# Revit family: Legrand XL³-S 630 16 Modules to the row
name_source: partatom
category: Equipement électrique
units: mm (PartAtom-declared; Revit-internal decimal feet)

## family parameters
Basée sur le plan de construction = Non
Configuration du panneau = Deux colonnes, circuits au sein
Cote de connecteur circulaire = Utiliser le diamètre
Couper avec des vides une fois chargée = Non
Numéro OmniClass = 23.80.30.11.17
Partagée = Non
Point de calcul de pièce = Non
Titre OmniClass = Distribution Boards and Control Panels
Toujours verticalement = Oui
Type d'élément = Tableau de raccordement

## types (11) — shared parameters
ETIM Class 6.0 = EC000261
Fabricant = Legrand
General Conditions of Use = https://export.legrand.com
IK = 08
IP = 40
Image du type = XL3S_630_16M_337581_p_230129.jpg
Material = Steel
RAL = 9003
URL = www.legrand.fr
depth = 249 mm  [stored 0.816929 ft]
depth installation zone = 703 mm  [stored 2.30643 ft]
distance before installation zone = 454 mm  [stored 1.4895 ft]
distance side installation zone = 249 mm  [stored 0.816929 ft]
door = Oui
finish kit = Non
finish kit 337960_337972 = Non
finish kit 337961_337972 = Non
finish kit 337962_337972 = Non
finish kit 337963_337972 = Non
finish kit 337964_337972 = Non
finish kit 337965_337972 = Non
finish kit 337966_337972 = Non
finish kit 337967_337972 = Non
finish kit 337968_337972 = Non
finish kit 337969_337972 = Non
finish kit 337970_337972 = Non
height Base = 100 mm  [stored 0.328084 ft]
left side panel = Oui
plinth = Oui
right side panel = Oui
width = 454 mm  [stored 1.4895 ft]
width installation zone = 952 mm  [stored 3.12336 ft]
zero-valued in all types: Elévation par défaut

## per-type parameters (varying)
- Distribution envelope - XL³ S 630 Métal - height 750 - 16 modules: Description=337521  Distribution envelope - XL³ S 630 Métal - height 750 - 16 modules; door 337641=Oui; door 337651=Non; door 337661=Non; door 337671=Non; door 337681=Non; door 337691=Non; door 337701=Non; door 337711=Non; door 337721=Non; door 337731=Non; door 337741=Non; envelope 337521=Oui; envelope 337531=Non; envelope 337541=Non; envelope 337551=Non; envelope 337561=Non; envelope 337571=Non; envelope 337581=Non; envelope 337591=Non; envelope 337601=Non; envelope 337611=Non; envelope 337621=Non; height=924 mm  [stored 3.0315 ft]; left side panel  337872=Non; left side panel 337862=Oui; left side panel 337863=Non; left side panel 337864=Non; left side panel 337865=Non; left side panel 337866=Non; left side panel 337867=Non; left side panel 337868=Non; left side panel 337869=Non; left side panel 337870=Non; left side panel 337871=Non; right side panel 337862=Oui; right side panel 337863=Non; right side panel 337864=Non; right side panel 337865=Non; right side panel 337866=Non; right side panel 337867=Non; right side panel 337868=Non; right side panel 337869=Non; right side panel 337870=Non; right side panel 337871=Non; right side panel 337872=Non
- Distribution envelope - XL³ S 630 Métal - height 900 - 16 modules: Description=337531  Distribution envelope - XL³ S 630 Métal - height 900 - 16 modules; door 337641=Non; door 337651=Oui; door 337661=Non; door 337671=Non; door 337681=Non; door 337691=Non; door 337701=Non; door 337711=Non; door 337721=Non; door 337731=Non; door 337741=Non; envelope 337521=Non; envelope 337531=Oui; envelope 337541=Non; envelope 337551=Non; envelope 337561=Non; envelope 337571=Non; envelope 337581=Non; envelope 337591=Non; envelope 337601=Non; envelope 337611=Non; envelope 337621=Non; height=1074 mm  [stored 3.52362 ft]; left side panel  337872=Non; left side panel 337862=Non; left side panel 337863=Oui; left side panel 337864=Non; left side panel 337865=Non; left side panel 337866=Non; left side panel 337867=Non; left side panel 337868=Non; left side panel 337869=Non; left side panel 337870=Non; left side panel 337871=Non; right side panel 337862=Non; right side panel 337863=Oui; right side panel 337864=Non; right side panel 337865=Non; right side panel 337866=Non; right side panel 337867=Non; right side panel 337868=Non; right side panel 337869=Non; right side panel 337870=Non; right side panel 337871=Non; right side panel 337872=Non
- Distribution envelope - XL³ S 630 Métal - height 1050 - 16 modules: Description=337541  Distribution envelope - XL³ S 630 Métal - height 1050 - 16 modules; door 337641=Non; door 337651=Non; door 337661=Oui; door 337671=Non; door 337681=Non; door 337691=Non; door 337701=Non; door 337711=Non; door 337721=Non; door 337731=Non; door 337741=Non; envelope 337521=Non; envelope 337531=Non; envelope 337541=Oui; envelope 337551=Non; envelope 337561=Non; envelope 337571=Non; envelope 337581=Non; envelope 337591=Non; envelope 337601=Non; envelope 337611=Non; envelope 337621=Non; height=1224 mm  [stored 4.01575 ft]; left side panel  337872=Non; left side panel 337862=Non; left side panel 337863=Non; left side panel 337864=Oui; left side panel 337865=Non; left side panel 337866=Non; left side panel 337867=Non; left side panel 337868=Non; left side panel 337869=Non; left side panel 337870=Non; left side panel 337871=Non; right side panel 337862=Non; right side panel 337863=Non; right side panel 337864=Oui; right side panel 337865=Non; right side panel 337866=Non; right side panel 337867=Non; right side panel 337868=Non; right side panel 337869=Non; right side panel 337870=Non; right side panel 337871=Non; right side panel 337872=Non
- Distribution envelope - XL³ S 630 Métal - height 1200 - 16 modules: Description=337551  Distribution envelope - XL³ S 630 Métal - height 1200 - 16 modules; door 337641=Non; door 337651=Non; door 337661=Non; door 337671=Oui; door 337681=Non; door 337691=Non; door 337701=Non; door 337711=Non; door 337721=Non; door 337731=Non; door 337741=Non; envelope 337521=Non; envelope 337531=Non; envelope 337541=Non; envelope 337551=Oui; envelope 337561=Non; envelope 337571=Non; envelope 337581=Non; envelope 337591=Non; envelope 337601=Non; envelope 337611=Non; envelope 337621=Non; height=1374 mm  [stored 4.50787 ft]; left side panel  337872=Non; left side panel 337862=Non; left side panel 337863=Non; left side panel 337864=Non; left side panel 337865=Oui; left side panel 337866=Non; left side panel 337867=Non; left side panel 337868=Non; left side panel 337869=Non; left side panel 337870=Non; left side panel 337871=Non; right side panel 337862=Non; right side panel 337863=Non; right side panel 337864=Non; right side panel 337865=Oui; right side panel 337866=Non; right side panel 337867=Non; right side panel 337868=Non; right side panel 337869=Non; right side panel 337870=Non; right side panel 337871=Non; right side panel 337872=Non
- Distribution envelope - XL³ S 630 Métal - height 1350 - 16 modules: Description=337561  Distribution envelope - XL³ S 630 Métal - height 1350 - 16 modules; door 337641=Non; door 337651=Non; door 337661=Non; door 337671=Non; door 337681=Oui; door 337691=Non; door 337701=Non; door 337711=Non; door 337721=Non; door 337731=Non; door 337741=Non; envelope 337521=Non; envelope 337531=Non; envelope 337541=Non; envelope 337551=Non; envelope 337561=Oui; envelope 337571=Non; envelope 337581=Non; envelope 337591=Non; envelope 337601=Non; envelope 337611=Non; envelope 337621=Non; height=1524 mm  [stored 5 ft]; left side panel  337872=Non; left side panel 337862=Non; left side panel 337863=Non; left side panel 337864=Non; left side panel 337865=Non; left side panel 337866=Oui; left side panel 337867=Non; left side panel 337868=Non; left side panel 337869=Non; left side panel 337870=Non; left side panel 337871=Non; right side panel 337862=Non; right side panel 337863=Non; right side panel 337864=Non; right side panel 337865=Non; right side panel 337866=Oui; right side panel 337867=Non; right side panel 337868=Non; right side panel 337869=Non; right side panel 337870=Non; right side panel 337871=Non; right side panel 337872=Non
- Distribution envelope - XL³ S 630 Métal - height 1500 - 16 modules: Description=337571  Distribution envelope - XL³ S 630 Métal - height 1500 - 16 modules; door 337641=Non; door 337651=Non; door 337661=Non; door 337671=Non; door 337681=Non; door 337691=Oui; door 337701=Non; door 337711=Non; door 337721=Non; door 337731=Non; door 337741=Non; envelope 337521=Non; envelope 337531=Non; envelope 337541=Non; envelope 337551=Non; envelope 337561=Non; envelope 337571=Oui; envelope 337581=Non; envelope 337591=Non; envelope 337601=Non; envelope 337611=Non; envelope 337621=Non; height=1674 mm  [stored 5.49213 ft]; left side panel  337872=Non; left side panel 337862=Non; left side panel 337863=Non; left side panel 337864=Non; left side panel 337865=Non; left side panel 337866=Non; left side panel 337867=Oui; left side panel 337868=Non; left side panel 337869=Non; left side panel 337870=Non; left side panel 337871=Non; right side panel 337862=Non; right side panel 337863=Non; right side panel 337864=Non; right side panel 337865=Non; right side panel 337866=Non; right side panel 337867=Oui; right side panel 337868=Non; right side panel 337869=Non; right side panel 337870=Non; right side panel 337871=Non; right side panel 337872=Non
- Distribution envelope - XL³ S 630 Métal - height 1650 - 16 modules: Description=337581  Distribution envelope - XL³ S 630 Métal - height 1650 - 16 modules; door 337641=Non; door 337651=Non; door 337661=Non; door 337671=Non; door 337681=Non; door 337691=Non; door 337701=Oui; door 337711=Non; door 337721=Non; door 337731=Non; door 337741=Non; envelope 337521=Non; envelope 337531=Non; envelope 337541=Non; envelope 337551=Non; envelope 337561=Non; envelope 337571=Non; envelope 337581=Oui; envelope 337591=Non; envelope 337601=Non; envelope 337611=Non; envelope 337621=Non; height=1824 mm  [stored 5.98425 ft]; left side panel  337872=Non; left side panel 337862=Non; left side panel 337863=Non; left side panel 337864=Non; left side panel 337865=Non; left side panel 337866=Non; left side panel 337867=Non; left side panel 337868=Oui; left side panel 337869=Non; left side panel 337870=Non; left side panel 337871=Non; right side panel 337862=Non; right side panel 337863=Non; right side panel 337864=Non; right side panel 337865=Non; right side panel 337866=Non; right side panel 337867=Non; right side panel 337868=Oui; right side panel 337869=Non; right side panel 337870=Non; right side panel 337871=Non; right side panel 337872=Non
- Distribution envelope - XL³ S 630 Métal - height 1800 - 16 modules: Description=337591  Distribution envelope - XL³ S 630 Métal - height 1800 - 16 modules; door 337641=Non; door 337651=Non; door 337661=Non; door 337671=Non; door 337681=Non; door 337691=Non; door 337701=Non; door 337711=Oui; door 337721=Non; door 337731=Non; door 337741=Non; envelope 337521=Non; envelope 337531=Non; envelope 337541=Non; envelope 337551=Non; envelope 337561=Non; envelope 337571=Non; envelope 337581=Non; envelope 337591=Oui; envelope 337601=Non; envelope 337611=Non; envelope 337621=Non; height=1974 mm  [stored 6.47638 ft]; left side panel  337872=Non; left side panel 337862=Non; left side panel 337863=Non; left side panel 337864=Non; left side panel 337865=Non; left side panel 337866=Non; left side panel 337867=Non; left side panel 337868=Non; left side panel 337869=Oui; left side panel 337870=Non; left side panel 337871=Non; right side panel 337862=Non; right side panel 337863=Non; right side panel 337864=Non; right side panel 337865=Non; right side panel 337866=Non; right side panel 337867=Non; right side panel 337868=Non; right side panel 337869=Oui; right side panel 337870=Non; right side panel 337871=Non; right side panel 337872=Non
- Distribution envelope - XL³ S 630 Métal - height 1950 - 16 modules: Description=337601  Distribution envelope - XL³ S 630 Métal - height 1950 - 16 modules; door 337641=Non; door 337651=Non; door 337661=Non; door 337671=Non; door 337681=Non; door 337691=Non; door 337701=Non; door 337711=Non; door 337721=Oui; door 337731=Non; door 337741=Non; envelope 337521=Non; envelope 337531=Non; envelope 337541=Non; envelope 337551=Non; envelope 337561=Non; envelope 337571=Non; envelope 337581=Non; envelope 337591=Non; envelope 337601=Oui; envelope 337611=Non; envelope 337621=Non; height=2124 mm  [stored 6.9685 ft]; left side panel  337872=Non; left side panel 337862=Non; left side panel 337863=Non; left side panel 337864=Non; left side panel 337865=Non; left side panel 337866=Non; left side panel 337867=Non; left side panel 337868=Non; left side panel 337869=Non; left side panel 337870=Oui; left side panel 337871=Non; right side panel 337862=Non; right side panel 337863=Non; right side panel 337864=Non; right side panel 337865=Non; right side panel 337866=Non; right side panel 337867=Non; right side panel 337868=Non; right side panel 337869=Non; right side panel 337870=Oui; right side panel 337871=Non; right side panel 337872=Non
- Distribution envelope - XL³ S 630 Métal - height 2100 - 16 modules: Description=337611  Distribution envelope - XL³ S 630 Métal - height 2100 - 16 modules; door 337641=Non; door 337651=Non; door 337661=Non; door 337671=Non; door 337681=Non; door 337691=Non; door 337701=Non; door 337711=Non; door 337721=Non; door 337731=Oui; door 337741=Non; envelope 337521=Non; envelope 337531=Non; envelope 337541=Non; envelope 337551=Non; envelope 337561=Non; envelope 337571=Non; envelope 337581=Non; envelope 337591=Non; envelope 337601=Non; envelope 337611=Oui; envelope 337621=Non; height=2274 mm  [stored 7.46063 ft]; left side panel  337872=Non; left side panel 337862=Non; left side panel 337863=Non; left side panel 337864=Non; left side panel 337865=Non; left side panel 337866=Non; left side panel 337867=Non; left side panel 337868=Non; left side panel 337869=Non; left side panel 337870=Non; left side panel 337871=Oui; right side panel 337862=Non; right side panel 337863=Non; right side panel 337864=Non; right side panel 337865=Non; right side panel 337866=Non; right side panel 337867=Non; right side panel 337868=Non; right side panel 337869=Non; right side panel 337870=Non; right side panel 337871=Oui; right side panel 337872=Non
- Distribution envelope - XL³ S 630 Métal - height 2250 - 16 modules: Description=337621  Distribution envelope - XL³ S 630 Métal - height 2250 - 16 modules; door 337641=Non; door 337651=Non; door 337661=Non; door 337671=Non; door 337681=Non; door 337691=Non; door 337701=Non; door 337711=Non; door 337721=Non; door 337731=Non; door 337741=Oui; envelope 337521=Non; envelope 337531=Non; envelope 337541=Non; envelope 337551=Non; envelope 337561=Non; envelope 337571=Non; envelope 337581=Non; envelope 337591=Non; envelope 337601=Non; envelope 337611=Non; envelope 337621=Oui; height=2424 mm  [stored 7.95276 ft]; left side panel  337872=Oui; left side panel 337862=Non; left side panel 337863=Non; left side panel 337864=Non; left side panel 337865=Non; left side panel 337866=Non; left side panel 337867=Non; left side panel 337868=Non; left side panel 337869=Non; left side panel 337870=Non; left side panel 337871=Non; right side panel 337862=Non; right side panel 337863=Non; right side panel 337864=Non; right side panel 337865=Non; right side panel 337866=Non; right side panel 337867=Non; right side panel 337868=Non; right side panel 337869=Non; right side panel 337870=Non; right side panel 337871=Non; right side panel 337872=Oui

note: [stored X ft] marks values corroborated as IEEE doubles in the binary element streams (Revit-internal decimal feet)
